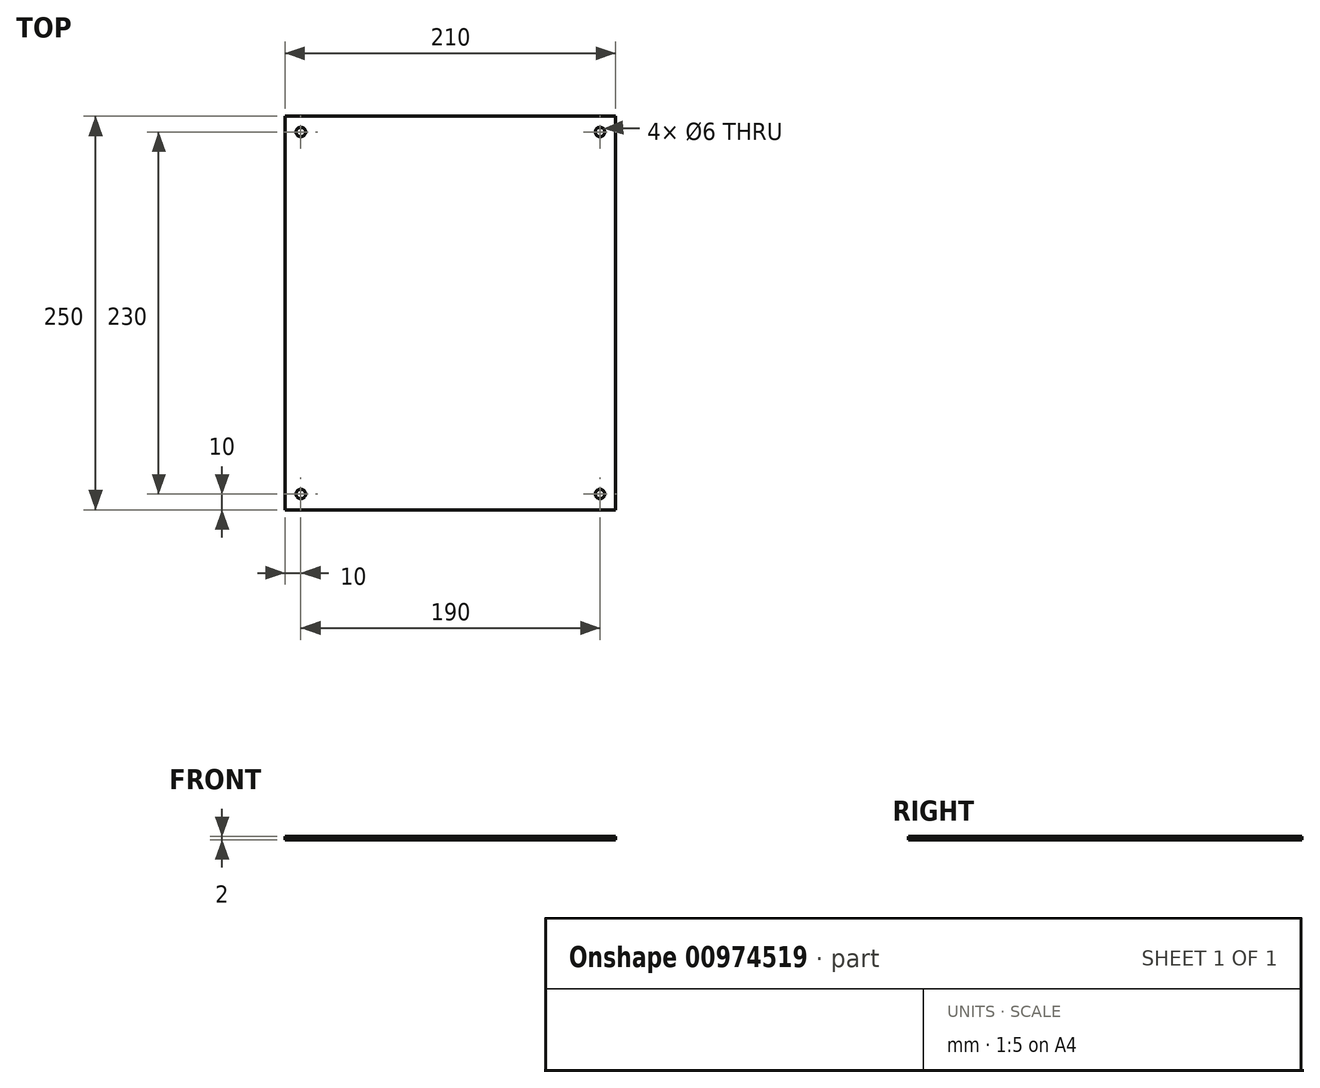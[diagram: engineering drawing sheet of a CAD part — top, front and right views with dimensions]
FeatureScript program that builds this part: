
annotation { "Feature Type Name" : "Feature", "Feature Type Description" : "" }
export const myFeature = defineFeature(function(context is Context, id is Id, definition is map)
    precondition{}
    {
        {
            var Q0;
            Q0=qCreatedBy(makeId("Top.planeOp"),FACE);
            var sketch = newSketch(context, id + "F0", { "sketchPlane" : qUnion([Q0])});
            skLineSegment(sketch, "E0.bottom", {"start": v(105, -125) * mm, "end": v(-105, -125) * mm});
            skLineSegment(sketch, "E0.top", {"start": v(105, 125) * mm, "end": v(-105, 125) * mm});
            skLineSegment(sketch, "E0.left", {"start": v(105, -125) * mm, "end": v(105, 125) * mm});
            skLineSegment(sketch, "E0.right", {"start": v(-105, -125) * mm, "end": v(-105, 125) * mm});
            skPoint(sketch, "E0.middle", {"position": v(0, 0) * mm});
            skSolve(sketch);
        }
        {
            var Q0;
            Q0 = qSketchRegion(id + "F0", true);
            extrude(context, id + "F1", {"entities" : qUnion([Q0]), "depth" : 2 * mm, "offsetDistance" : 25 * mm});
        }
        {
            var Q0;
            Q0=makeQuery(id+"F1.opExtrude","CAP_FACE",FACE,{"disambiguationData":[OSD([sQuery(id+"F0.wireOp",EDGE,"E0.bottom"),sQuery(id+"F0.wireOp",EDGE,"E0.top"),sQuery(id+"F0.wireOp",EDGE,"E0.left"),sQuery(id+"F0.wireOp",EDGE,"E0.right")])],"isStart":false});
            var sketch = newSketch(context, id + "F2", { "sketchPlane" : qUnion([Q0])});
            skPoint(sketch, "E1", {"position": v(-95, 115) * mm});
            skPoint(sketch, "E2", {"position": v(95, 115) * mm});
            skPoint(sketch, "E3", {"position": v(95, -115) * mm});
            skPoint(sketch, "E4", {"position": v(-95, -115) * mm});
            skSolve(sketch);
        }
        {
            var Q0;
            Q0=sQuery(id+"F2.wireOp",VERTEX,"E1");
            var Q1;
            Q1=sQuery(id+"F2.wireOp",VERTEX,"E2");
            var Q2;
            Q2=sQuery(id+"F2.wireOp",VERTEX,"E3");
            var Q3;
            Q3=sQuery(id+"F2.wireOp",VERTEX,"E4");
            var Q4;
            Q4=makeQuery(id+"F1.opExtrude","SWEPT_BODY",BODY,{"disambiguationData":[OSD([sQuery(id+"F0.wireOp",EDGE,"E0.bottom"),sQuery(id+"F0.wireOp",EDGE,"E0.top"),sQuery(id+"F0.wireOp",EDGE,"E0.left"),sQuery(id+"F0.wireOp",EDGE,"E0.right")])]});
            hole(context, id + "F3", {"style" : HoleStyle.SIMPLE, "endStyle" : HoleEndStyle.THROUGH, "holeDiameter" : 6 * mm, "majorDiameter" : 5 * mm, "isTappedThrough" : true, "tappedDepth" : 12 * mm, "tapClearance" : 3, "locations" : qUnion([Q0, Q1, Q2, Q3]), "scope" : qUnion([Q4])});
        }
    });
